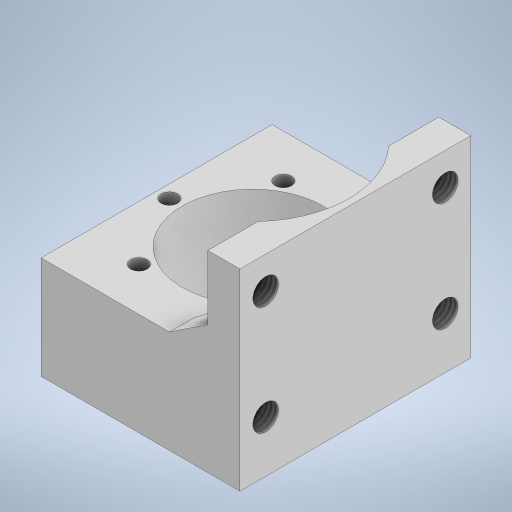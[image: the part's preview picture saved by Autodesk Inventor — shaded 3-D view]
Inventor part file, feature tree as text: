
AUTODESK INVENTOR PART (.ipt)
format: ipt  version: 2024 (Build 280153000, 153)  size: 307,712 bytes
history: native  units: mm
features: extrude x6, sketch x6, thread x4
ambient origin geometry x8: Origin, YZ Plane, XZ Plane, XY Plane, X Axis, Y Axis, Z Axis, Center Point
bodies: Solid1 (feature_tree)
feature tree (16):
  extrude  "Extrusion1"  Depth=15.0mm
  extrude  "Extrusion2"  Depth=18.0mm
  extrude  "Extrusion3"  Depth=30.0mm TaperAngle=0.0deg
  extrude  "Extrusion4"  Depth=30.0mm TaperAngle=0.0deg
  extrude  "Extrusion5"  Depth=2.0mm TaperAngle=0.0deg
  thread  "Thread1"  [1 undecoded]
  thread  "Thread2"  [1 undecoded]
  thread  "Thread3"  [1 undecoded]
  thread  "Thread4"  [1 undecoded]
  extrude  "Extrusion6"  Depth=30.0mm
  sketch  "Sketch1"  dims[d0=22.0mm d1=15.0mm]
  sketch  "Sketch3"  dims[d2=16.0mm d3=18.0mm]
  sketch  "Sketch4"  dims[d4=18.0mm d5=30.0mm d6=0.0mm]
  sketch  "Sketch5"  dims[d7=16.0mm d8=30.0mm d9=0.0mm]
  sketch  "Sketch6"  dims[d10=14.0mm d11=0.0mm d12=2.0mm d13=0.0mm d14=200.0mm d15=0.0mm d16=5.0mm d17=0.0mm d18=5.0mm d19=0.0mm d20=30.0mm d21=0.0mm]
  sketch  "Sketch7"  dims[d22=30.0mm d23=0.0mm d24=30.0mm d25=2.6mm d26=13.0mm d27=60.0mm d29=360.0deg d31=200.0mm d32=0.0mm]
note: 4 required parameter values undecoded (feature->parameter linkage not recoverable at this tier; creation-order binding heuristic only, values carry confidence <= 0.55)
